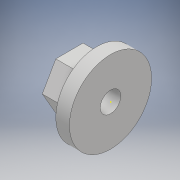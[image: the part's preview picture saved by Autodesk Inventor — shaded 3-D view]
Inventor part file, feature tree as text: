
AUTODESK INVENTOR PART (.ipt)
format: ipt  version: 2018 (Build 220112000, 112)  size: 121,856 bytes
history: native  units: mm
features: sketch x5, extrude x4
ambient origin geometry x8: Origin, YZ Plane, XZ Plane, XY Plane, X Axis, Y Axis, Z Axis, Center Point
bodies: Solid1 (feature_tree)
feature tree (9):
  extrude  "Extrusion1"  Depth=4.0mm TaperAngle=0.0deg
  extrude  "Extrusion2"  Depth=2.0mm
  sketch  "Sketch3"  dims[d6=2.0mm d7=0.0mm d8=3.0mm]
  extrude  "Extrusion3"  Depth=2.0mm
  extrude  "Extrusion4"  [1 undecoded]
  sketch  "Sketch1"  dims[d0=4.0mm d1=4.0mm d2=0.0mm]
  sketch  "Sketch2"  dims[d3=2.0mm d4=0.0mm d5=12.0mm]
  sketch  "Sketch4"  dims[d9=6.0mm d10=0.0mm]
  sketch  "Sketch5"
note: 1 required parameter value undecoded (feature->parameter linkage not recoverable at this tier; creation-order binding heuristic only, values carry confidence <= 0.55)
